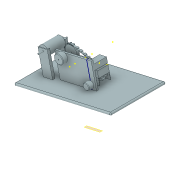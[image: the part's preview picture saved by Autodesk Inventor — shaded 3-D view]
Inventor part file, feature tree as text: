
AUTODESK INVENTOR PART (.ipt)
format: ipt  version: 2019 (Build 230136000, 136)  size: 878,592 bytes
history: mixed  units: in
note: dims shown in document units (in); Inventor stores cm internally (conversion verified against a paired STEP export)
features: sketch x59, extrude x34, fillet x6, plane x4, imported_body x2, chamfer x1
ambient origin geometry x8: Origin, YZ Plane, XZ Plane, XY Plane, X Axis, Y Axis, Z Axis, Center Point
bodies: Solid1 (imported_parasolid)
feature tree (106):
  plane  "Work Plane1"
  extrude  "Extrusion1"  Depth=0.3937in TaperAngle=0.0deg
  sketch  "Sketch2"  dims[d3=0.1378in d4=0.1969in d5=0.0in d6=0.0in d7=0.3937in d8=0.0in]
  extrude  "Extrusion2"  Depth=0.3937in TaperAngle=0.0deg
  sketch  "Sketch4"  dims[d13=0.3937in d14=0.0in d15=0.3937in d16=0.0in]
  sketch  "Sketch5"  dims[d17=0.3937in d18=0.0in d19=0.3937in d20=0.0in]
  extrude  "Extrusion3"  Depth=0.3937in TaperAngle=0.0deg
  extrude  "Extrusion4"  Depth=0.3937in TaperAngle=0.0deg
  extrude  "Extrusion5"  Depth=0.3937in TaperAngle=0.0deg
  extrude  "Extrusion6"  Depth=0.3937in TaperAngle=0.0deg
  sketch  "Sketch10"  dims[d37=0.7874in d38=0.0in d39=0.3937in d40=0.0in]
  sketch  "Sketch11"  dims[d41=0.7874in d42=0.0in d43=1.1811in d44=0.0in]
  sketch  "Sketch12"  dims[d45=1.1811in d46=0.0in d47=0.7874in d48=0.0in]
  sketch  "Sketch13"  dims[d49=0.1969in d50=0.1969in]
  extrude  "Extrusion7"  Depth=0.3937in
  extrude  "Extrusion8"  Depth=3.937in TaperAngle=0.0deg
  extrude  "Extrusion9"  Depth=0.7874in TaperAngle=0.0deg
  extrude  "Extrusion10"  Depth=0.3937in TaperAngle=0.0deg
  extrude  "Extrusion11"  Depth=1.1811in TaperAngle=0.0deg
  extrude  "Extrusion12"  Depth=0.7874in TaperAngle=0.0deg
  plane  "Work Plane3"
  extrude  "Extrusion13"  Depth=0.1969in
  extrude  "Extrusion14"  Depth=0.1969in
  extrude  "Extrusion15"  Depth=1.378in TaperAngle=0.0deg
  extrude  "Extrusion16"  Depth=0.1417in
  extrude  "Extrusion17"  Depth=1.9685in TaperAngle=0.0deg
  extrude  "Extrusion18"  Depth=0.7874in TaperAngle=0.0deg
  extrude  "Extrusion19"  Depth=0.315in TaperAngle=0.0deg
  extrude  "Extrusion20"  Depth=0.0787in
  sketch  "Sketch28"
  extrude  "Extrusion21"  Depth=0.3937in
  extrude  "Extrusion22"  Depth=0.3937in
  sketch  "Sketch31"
  sketch  "Sketch32"
  sketch  "Sketch33"
  fillet  "Fillet1"  Radius=3.937in
  fillet  "Fillet2"  Radius=2.7559in
  fillet  "Fillet3"  Radius=3.937in
  fillet  "Fillet4"  Radius=0.7874in
  sketch  "Sketch34"
  extrude  "Extrusion23"  [1 undecoded]
  plane  "Work Plane4"
  extrude  "Extrusion24"  [1 undecoded]
  fillet  "Fillet5"  [1 undecoded]
  sketch  "Sketch37"
  sketch  "Sketch38"
  sketch  "Sketch39"
  sketch  "Sketch40"
  sketch  "Sketch41"
  extrude  "Extrusion25"  [1 undecoded]
  sketch  "Sketch43"
  extrude  "Extrusion26"  [1 undecoded]
  extrude  "Extrusion27"  [1 undecoded]
  sketch  "Sketch46"
  extrude  "Extrusion28"  [1 undecoded]
  chamfer  "Chamfer1"  [1 undecoded]
  extrude  "Extrusion29"  [1 undecoded]
  extrude  "Extrusion30"  [1 undecoded]
  fillet  "Fillet6"  [1 undecoded]
  sketch  "Sketch50"
  sketch  "Sketch51"
  sketch  "Sketch52"
  sketch  "Sketch53"
  extrude  "Extrusion31"  [1 undecoded]
  sketch  "Sketch55"
  extrude  "Extrusion32"  [1 undecoded]
  extrude  "Extrusion33"  [1 undecoded]
  extrude  "Extrusion34"  [1 undecoded]
  sketch  "Sketch59"
  sketch  "Sketch1"  dims[d0=0.0in d1=0.3937in d2=0.0in]
  sketch  "Sketch3"  dims[d9=0.3937in d10=0.0in d11=0.3937in d12=0.0in]
  sketch  "Sketch6"  dims[d21=0.3937in d22=0.0in d23=0.3937in d24=0.0in]
  sketch  "Sketch7"  dims[d25=0.3937in d26=0.0in d27=-7.874in d28=5.9055in]
  sketch  "Sketch8"  dims[d29=0.3937in d30=0.0in d31=3.937in d32=0.0in]
  sketch  "Sketch9"  dims[d33=0.7874in d34=0.0in d35=0.7874in d36=0.0in]
  sketch  "Sketch14"  dims[d51=0.1969in d52=0.1969in]
  sketch  "Sketch15"  dims[d53=0.4173in d54=1.378in d55=0.0in]
  sketch  "Sketch16"  dims[d56=0.6299in d57=0.0in d58=0.1417in]
  sketch  "Sketch17"  dims[d60=2.3622in d61=0.0in d62=1.9685in d63=0.0in]
  sketch  "Sketch18"  dims[d64=0.6299in d65=0.0in d66=0.7874in d67=0.0in]
  sketch  "Sketch19"  dims[d68=0.0787in d69=0.0492in d70=45.0deg d71=0.315in d72=0.0in]
  plane  "Work Plane2"
  sketch  "Sketch20"  dims[d73=0.7874in d74=0.0in d75=0.0787in]
  sketch  "Sketch21"  dims[d76=1.5748in d77=0.3937in]
  sketch  "Sketch22"  dims[d78=1.5748in d79=0.3937in d80=3.937in d81=0.0in d82=2.7559in d83=0.0in d84=3.937in d85=0.0in d86=0.7874in d87=0.0in]
  sketch  "Sketch23"
  sketch  "Sketch24"
  sketch  "Sketch25"
  sketch  "Sketch26"
  sketch  "Sketch27"
  sketch  "Sketch29"
  sketch  "Sketch30"
  sketch  "Sketch35"
  sketch  "Sketch36"
  sketch  "Sketch42"
  sketch  "Sketch44"
  sketch  "Sketch45"
  sketch  "Sketch47"
  sketch  "Sketch48"
  sketch  "Sketch49"
  sketch  "Sketch54"
  sketch  "Sketch56"
  sketch  "Sketch57"
  sketch  "Sketch58"
  imported_body  "Base1"
  imported_body  NMx_Import_Brep_tag  [imported B-rep: ~54 faces, bbox_mm=[396.369894, 166.187241, 221.510673]]
note: 15 required parameter values undecoded (feature->parameter linkage not recoverable at this tier; creation-order binding heuristic only, values carry confidence <= 0.55)
